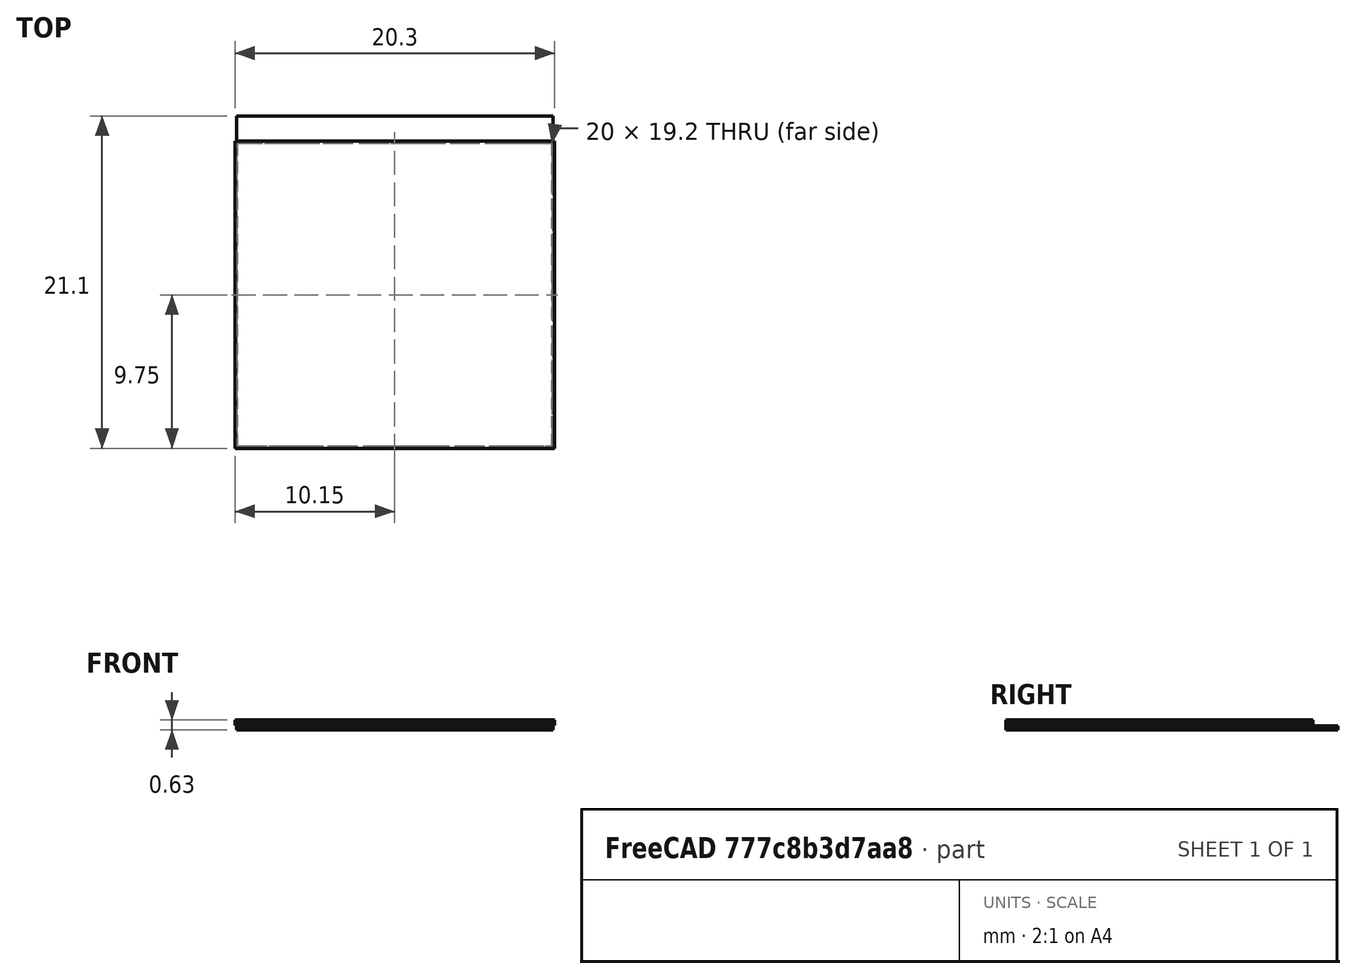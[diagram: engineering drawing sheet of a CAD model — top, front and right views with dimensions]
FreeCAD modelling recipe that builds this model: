
FCSTD DOCUMENT  (FreeCAD 0.17R13541 (Git))
Label: singlethick
License: All rights reserved
LicenseURL: http://en.wikipedia.org/wiki/All_rights_reserved
objects: Sketcher::SketchObject×10, PartDesign::Pad×10, PartDesign::Body×10, PartDesign::ShapeBinder×9, App::MaterialObjectPython×7, Part::FeaturePython×2, Fem::FemSolverObjectPython×1, Fem::ConstraintInitialTemperature×1, Fem::FemMeshObjectPython×1, Fem::ConstraintHeatflux×1, Fem::ConstraintFixed×1, Fem::FemAnalysis×1
note: 51 computed .brp shape members not serialized (recipe doc carries the construction recipe); baked Part::Feature solids carry a one-line shape summary decoded from their .brp

FEATURE [Sketcher::SketchObject] Sketch
  MapMode = 5
  Support = -> [XY_Plane]
  sketch-geometry (4):
    g0: LineSegment StartX=0 StartY=0 StartZ=0 EndX=20.1 EndY=0 EndZ=0
    g1: LineSegment StartX=20.1 StartY=0 StartZ=0 EndX=20.1 EndY=21.1 EndZ=0
    g2: LineSegment StartX=20.1 StartY=21.1 StartZ=0 EndX=0 EndY=21.1 EndZ=0
    g3: LineSegment StartX=0 StartY=21.1 StartZ=0 EndX=0 EndY=0 EndZ=0
  constraints (11):
    c: Coincident(g0,g1)
    c: Coincident(g1,g2)
    c: Coincident(g2,g3)
    c: Coincident(g3,g0)
    c: Horizontal(g0)
    c: Horizontal(g2)
    c: Vertical(g1)
    c: Vertical(g3)
    c: Coincident(g0,g-1)
    c: DistanceX(g0,g0) = 20.1
    c: DistanceY(g3,g3) = 21.1
FEATURE [PartDesign::Pad] Pad
  Length = 0.15
  Length2 = 100
  Profile = -> Sketch
  Type = 0
FEATURE [PartDesign::Body] Body
  Group = -> [Sketch,Pad]
  Origin = -> Origin
  Tip = -> Pad
FEATURE [PartDesign::ShapeBinder] CopyPad
  Placement = pos=(0,0,0.15) rot=(0,0,1;0rad)
FEATURE [Sketcher::SketchObject] Sketch001
  MapMode = 5
  Placement = pos=(0,0,0.15) rot=(0,0,1;0rad)
  Support = -> [CopyPad]
  sketch-geometry (4):
    g0: LineSegment StartX=0.05 StartY=0.15 StartZ=0 EndX=20.05 EndY=0.15 EndZ=0
    g1: LineSegment StartX=20.05 StartY=0.15 StartZ=0 EndX=20.05 EndY=19.35 EndZ=0
    g2: LineSegment StartX=20.05 StartY=19.35 StartZ=0 EndX=0.05 EndY=19.35 EndZ=0
    g3: LineSegment StartX=0.05 StartY=19.35 StartZ=0 EndX=0.05 EndY=0.15 EndZ=0
  constraints (12):
    c: Coincident(g0,g1)
    c: Coincident(g1,g2)
    c: Coincident(g2,g3)
    c: Coincident(g3,g0)
    c: Horizontal(g0)
    c: Horizontal(g2)
    c: Vertical(g1)
    c: Vertical(g3)
    c: DistanceY(g-1,g0) = 0.15
    c: DistanceX(g-1,g0) = 0.05
    c: DistanceX(g0,g0) = 20
    c: DistanceY(g3,g3) = 19.2
FEATURE [PartDesign::Pad] Pad001
  Length = 0.025
  Length2 = 100
  Placement = pos=(0,0,0.15) rot=(0,0,1;0rad)
  Profile = -> Sketch001
  Type = 0
FEATURE [PartDesign::Body] Body001
  Group = -> [CopyPad,Sketch001,Pad001]
  Origin = -> Origin001
  Tip = -> Pad001
FEATURE [PartDesign::ShapeBinder] CopyPad001
  Placement = pos=(0,0,0.025) rot=(0,0,1;0rad)
FEATURE [Sketcher::SketchObject] Sketch002
  MapMode = 5
  Placement = pos=(0,0,0.175) rot=(0,0,1;0rad)
  Support = -> [CopyPad001]
  sketch-geometry (4):
    g0: LineSegment StartX=-0.1 StartY=0 StartZ=0 EndX=20.2 EndY=0 EndZ=0
    g1: LineSegment StartX=20.2 StartY=0 StartZ=0 EndX=20.2 EndY=19.5 EndZ=0
    g2: LineSegment StartX=20.2 StartY=19.5 StartZ=0 EndX=-0.1 EndY=19.5 EndZ=0
    g3: LineSegment StartX=-0.1 StartY=19.5 StartZ=0 EndX=-0.1 EndY=0 EndZ=0
  constraints (12):
    c: Coincident(g0,g1)
    c: Coincident(g1,g2)
    c: Coincident(g2,g3)
    c: Coincident(g3,g0)
    c: Horizontal(g0)
    c: Horizontal(g2)
    c: Vertical(g1)
    c: Vertical(g3)
    c: DistanceY(g0,g-1) = 0
    c: DistanceX(g0,g-1) = 0.1
    c: DistanceX(g0,g0) = 20.3
    c: DistanceY(g3,g3) = 19.5
FEATURE [PartDesign::Pad] Pad002
  Length = 0.15
  Length2 = 100
  Placement = pos=(0,0,0.025) rot=(0,0,1;0rad)
  Profile = -> Sketch002
  Type = 0
FEATURE [PartDesign::Body] Body002
  Group = -> [CopyPad001,Sketch002,Pad002]
  Origin = -> Origin002
  Tip = -> Pad002
FEATURE [PartDesign::ShapeBinder] CopyPad002
  Placement = pos=(0,0,0.15) rot=(0,0,1;0rad)
FEATURE [Sketcher::SketchObject] Sketch003
  MapMode = 5
  Placement = pos=(0,0,0.325) rot=(0,0,1;0rad)
  Support = -> [CopyPad002]
  sketch-geometry (4):
    g0: LineSegment StartX=-0.1 StartY=0 StartZ=0 EndX=20.2 EndY=0 EndZ=0
    g1: LineSegment StartX=20.2 StartY=0 StartZ=0 EndX=20.2 EndY=19.5 EndZ=0
    g2: LineSegment StartX=20.2 StartY=19.5 StartZ=0 EndX=-0.1 EndY=19.5 EndZ=0
    g3: LineSegment StartX=-0.1 StartY=19.5 StartZ=0 EndX=-0.1 EndY=0 EndZ=0
  constraints (12):
    c: Coincident(g0,g1)
    c: Coincident(g1,g2)
    c: Coincident(g2,g3)
    c: Coincident(g3,g0)
    c: Horizontal(g0)
    c: Horizontal(g2)
    c: Vertical(g1)
    c: Vertical(g3)
    c: DistanceY(g0,g-1) = 0
    c: DistanceX(g0,g-1) = 0.1
    c: DistanceX(g0,g0) = 20.3
    c: DistanceY(g3,g3) = 19.5
FEATURE [PartDesign::Pad] Pad003
  Length = 0.05
  Length2 = 100
  Placement = pos=(0,0,0.15) rot=(0,0,1;0rad)
  Profile = -> Sketch003
  Type = 0
FEATURE [PartDesign::Body] Body003
  Group = -> [CopyPad002,Sketch003,Pad003]
  Origin = -> Origin003
  Tip = -> Pad003
FEATURE [PartDesign::ShapeBinder] CopyPad003
  Placement = pos=(0,0,0.05) rot=(0,0,1;0rad)
FEATURE [Sketcher::SketchObject] Sketch004
  MapMode = 5
  Placement = pos=(0,0,0.375) rot=(0,0,1;0rad)
  Support = -> [CopyPad003]
  sketch-geometry (4):
    g0: LineSegment StartX=-0.1 StartY=0 StartZ=0 EndX=20.2 EndY=0 EndZ=0
    g1: LineSegment StartX=20.2 StartY=0 StartZ=0 EndX=20.2 EndY=19.5 EndZ=0
    g2: LineSegment StartX=20.2 StartY=19.5 StartZ=0 EndX=-0.1 EndY=19.5 EndZ=0
    g3: LineSegment StartX=-0.1 StartY=19.5 StartZ=0 EndX=-0.1 EndY=0 EndZ=0
  constraints (12):
    c: Coincident(g0,g1)
    c: Coincident(g1,g2)
    c: Coincident(g2,g3)
    c: Coincident(g3,g0)
    c: Horizontal(g0)
    c: Horizontal(g2)
    c: Vertical(g1)
    c: Vertical(g3)
    c: DistanceX(g0,g-1) = 0.1
    c: DistanceY(g0,g-1) = 0
    c: DistanceX(g0,g0) = 20.3
    c: DistanceY(g3,g3) = 19.5
FEATURE [PartDesign::Pad] Pad004
  Length = 0.0225
  Length2 = 100
  Placement = pos=(0,0,0.05) rot=(0,0,1;0rad)
  Profile = -> Sketch004
  Type = 0
FEATURE [PartDesign::Body] Body004
  Group = -> [CopyPad003,Sketch004,Pad004]
  Origin = -> Origin004
  Tip = -> Pad004
FEATURE [PartDesign::ShapeBinder] CopyPad004
  Placement = pos=(0,0,0.0225) rot=(0,0,1;0rad)
FEATURE [Sketcher::SketchObject] Sketch005
  MapMode = 5
  Placement = pos=(0,0,0.3975) rot=(0,0,1;0rad)
  Support = -> [CopyPad004]
  sketch-geometry (4):
    g0: LineSegment StartX=-0.1 StartY=0 StartZ=0 EndX=20.2 EndY=0 EndZ=0
    g1: LineSegment StartX=20.2 StartY=0 StartZ=0 EndX=20.2 EndY=19.5 EndZ=0
    g2: LineSegment StartX=20.2 StartY=19.5 StartZ=0 EndX=-0.1 EndY=19.5 EndZ=0
    g3: LineSegment StartX=-0.1 StartY=19.5 StartZ=0 EndX=-0.1 EndY=0 EndZ=0
  constraints (12):
    c: Coincident(g0,g1)
    c: Coincident(g1,g2)
    c: Coincident(g2,g3)
    c: Coincident(g3,g0)
    c: Horizontal(g0)
    c: Horizontal(g2)
    c: Vertical(g1)
    c: Vertical(g3)
    c: DistanceY(g0,g-1) = 0
    c: DistanceX(g0,g-1) = 0.1
    c: DistanceX(g0,g0) = 20.3
    c: DistanceY(g3,g3) = 19.5
FEATURE [PartDesign::Pad] Pad005
  Length = 0.0175
  Length2 = 100
  Placement = pos=(0,0,0.0225) rot=(0,0,1;0rad)
  Profile = -> Sketch005
  Type = 0
FEATURE [PartDesign::Body] Body005
  Group = -> [CopyPad004,Sketch005,Pad005]
  Origin = -> Origin005
  Tip = -> Pad005
FEATURE [PartDesign::ShapeBinder] CopyPad005
  Placement = pos=(0,0,0.0175) rot=(0,0,1;0rad)
FEATURE [Sketcher::SketchObject] Sketch006
  MapMode = 5
  Placement = pos=(0,0,0.415) rot=(0,0,1;0rad)
  Support = -> [CopyPad005]
  sketch-geometry (4):
    g0: LineSegment StartX=-0.1 StartY=0 StartZ=0 EndX=20.2 EndY=0 EndZ=0
    g1: LineSegment StartX=20.2 StartY=0 StartZ=0 EndX=20.2 EndY=19.5 EndZ=0
    g2: LineSegment StartX=20.2 StartY=19.5 StartZ=0 EndX=-0.1 EndY=19.5 EndZ=0
    g3: LineSegment StartX=-0.1 StartY=19.5 StartZ=0 EndX=-0.1 EndY=0 EndZ=0
  constraints (12):
    c: Coincident(g0,g1)
    c: Coincident(g1,g2)
    c: Coincident(g2,g3)
    c: Coincident(g3,g0)
    c: Horizontal(g0)
    c: Horizontal(g2)
    c: Vertical(g1)
    c: Vertical(g3)
    c: DistanceY(g0,g-1) = 0
    c: DistanceX(g0,g-1) = 0.1
    c: DistanceX(g0,g0) = 20.3
    c: DistanceY(g3,g3) = 19.5
FEATURE [PartDesign::Pad] Pad006
  Length = 0.07
  Length2 = 100
  Placement = pos=(0,0,0.0175) rot=(0,0,1;0rad)
  Profile = -> Sketch006
  Type = 0
FEATURE [PartDesign::Body] Body006
  Group = -> [CopyPad005,Sketch006,Pad006]
  Origin = -> Origin006
  Tip = -> Pad006
FEATURE [PartDesign::ShapeBinder] CopyPad008
FEATURE [Sketcher::SketchObject] Sketch009
  MapMode = 5
  Placement = pos=(0,0,0) rot=(1,0,0;3.14159rad)
  Support = -> [CopyPad008]
  sketch-geometry (4):
    g0: LineSegment StartX=0 StartY=0 StartZ=0 EndX=20.1 EndY=0 EndZ=0
    g1: LineSegment StartX=20.1 StartY=0 StartZ=0 EndX=20.1 EndY=-21.1 EndZ=0
    g2: LineSegment StartX=20.1 StartY=-21.1 StartZ=0 EndX=0 EndY=-21.1 EndZ=0
    g3: LineSegment StartX=0 StartY=-21.1 StartZ=0 EndX=0 EndY=0 EndZ=0
  constraints (11):
    c: Coincident(g0,g1)
    c: Coincident(g1,g2)
    c: Coincident(g2,g3)
    c: Coincident(g3,g0)
    c: Horizontal(g0)
    c: Horizontal(g2)
    c: Vertical(g1)
    c: Vertical(g3)
    c: Coincident(g0,g-1)
    c: DistanceX(g2,g2) = 20.1
    c: DistanceY(g3,g3) = 21.1
FEATURE [PartDesign::Pad] Pad009
  Length = 0.1
  Length2 = 100
  Profile = -> Sketch009
  Type = 0
FEATURE [PartDesign::Body] Body009
  Group = -> [CopyPad008,Sketch009,Pad009]
  Origin = -> Origin009
  Tip = -> Pad009
FEATURE [Fem::FemSolverObjectPython] CalculiXccxTools  # FEM object (typed FeaturePython)
  AnalysisType = 2
  BeamShellResultOutput3D = false
  EigenmodeHighLimit = 1000000
  EigenmodeLowLimit = 0
  EigenmodesCount = 10
  GeometricalNonlinearity = 0
  IterationsControlParameterCutb = 0.25,0.5,0.75,0.85,,,1.5,
  IterationsControlParameterIter = 4,8,9,200,10,400,,200,,
  IterationsControlParameterTimeUse = false
  IterationsThermoMechMaximum = 2000
  IterationsUserDefinedIncrementations = false
  IterationsUserDefinedTimeStepLength = false
  MaterialNonlinearity = 0
  MatrixSolverType = 0
  SplitInputWriter = false
  ThermoMechSteadyState = true
  TimeEnd = 1
  TimeInitialStep = 0.01
FEATURE [Fem::ConstraintInitialTemperature] FemConstraintInitialTemperature
  NormalDirection = (0,0,1)
  initialTemperature = 300
FEATURE [PartDesign::ShapeBinder] CopyPad006
  Placement = pos=(0,0,0.07) rot=(0,0,1;0rad)
FEATURE [Sketcher::SketchObject] Sketch010
  MapMode = 5
  Placement = pos=(0,0,0.485) rot=(0,0,1;0rad)
  Support = -> [CopyPad006]
  sketch-geometry (4):
    g0: LineSegment StartX=-0.1 StartY=0 StartZ=0 EndX=20.2 EndY=0 EndZ=0
    g1: LineSegment StartX=20.2 StartY=0 StartZ=0 EndX=20.2 EndY=19.5 EndZ=0
    g2: LineSegment StartX=20.2 StartY=19.5 StartZ=0 EndX=-0.1 EndY=19.5 EndZ=0
    g3: LineSegment StartX=-0.1 StartY=19.5 StartZ=0 EndX=-0.1 EndY=0 EndZ=0
  constraints (12):
    c: Coincident(g0,g1)
    c: Coincident(g1,g2)
    c: Coincident(g2,g3)
    c: Coincident(g3,g0)
    c: Horizontal(g0)
    c: Horizontal(g2)
    c: Vertical(g1)
    c: Vertical(g3)
    c: DistanceY(g0,g-1) = 0
    c: DistanceX(g0,g-1) = 0.1
    c: DistanceX(g0,g0) = 20.3
    c: DistanceY(g1,g1) = 19.5
FEATURE [PartDesign::Pad] Pad010
  Length = 0.0175
  Length2 = 100
  Placement = pos=(0,0,0.07) rot=(0,0,1;0rad)
  Profile = -> Sketch010
  Type = 0
FEATURE [PartDesign::Body] Body010
  Group = -> [CopyPad006,Sketch010,Pad010]
  Origin = -> Origin010
  Tip = -> Pad010
FEATURE [PartDesign::ShapeBinder] CopyPad010
  Placement = pos=(0,0,0.0175) rot=(0,0,1;0rad)
FEATURE [Sketcher::SketchObject] Sketch011
  MapMode = 5
  Placement = pos=(0,0,0.5025) rot=(0,0,1;0rad)
  Support = -> [CopyPad010]
  sketch-geometry (4):
    g0: LineSegment StartX=-0.1 StartY=0 StartZ=0 EndX=20.2 EndY=0 EndZ=0
    g1: LineSegment StartX=20.2 StartY=0 StartZ=0 EndX=20.2 EndY=19.5 EndZ=0
    g2: LineSegment StartX=20.2 StartY=19.5 StartZ=0 EndX=-0.1 EndY=19.5 EndZ=0
    g3: LineSegment StartX=-0.1 StartY=19.5 StartZ=0 EndX=-0.1 EndY=0 EndZ=0
  constraints (12):
    c: Coincident(g0,g1)
    c: Coincident(g1,g2)
    c: Coincident(g2,g3)
    c: Coincident(g3,g0)
    c: Horizontal(g0)
    c: Horizontal(g2)
    c: Vertical(g1)
    c: Vertical(g3)
    c: DistanceY(g0,g-1) = 0
    c: DistanceX(g0,g-1) = 0.1
    c: DistanceX(g0,g0) = 20.3
    c: DistanceY(g3,g3) = 19.5
FEATURE [PartDesign::Pad] Pad011
  Length = 0.0225
  Length2 = 100
  Placement = pos=(0,0,0.0175) rot=(0,0,1;0rad)
  Profile = -> Sketch011
  Type = 0
FEATURE [PartDesign::Body] Body011
  Group = -> [CopyPad010,Sketch011,Pad011]
  Origin = -> Origin011
  Tip = -> Pad011
FEATURE [Part::FeaturePython] BooleanFragments  # WARN: FeaturePython — macro-defined, semantics opaque (R4)
  Mode = 2
  Objects = -> [Body009,Body011,Body010,Body006,Body005,Body004,Body003,Body002,Body001,Body]
  Tolerance = 0
FEATURE [Part::FeaturePython] CompoundFilter  # WARN: FeaturePython — macro-defined, semantics opaque (R4)
  Base = -> BooleanFragments
  FilterType = 3
  Invert = false
  OverrideMaxVal = 0
  WindowFrom = 80
  WindowTo = 100
FEATURE [Fem::FemMeshObjectPython] FEMMeshGmsh  # FEM object (typed FeaturePython)
  Algorithm2D = 0
  Algorithm3D = 0
  CharacteristicLengthMax = 2
  CharacteristicLengthMin = 0
  CoherenceMesh = true
  ElementDimension = 0
  ElementOrder = 1
  GeometryTolerance = 1e-06
  GroupsOfNodes = false
  HighOrderOptimize = false
  OptimizeNetgen = false
  OptimizeStd = true
  Part = -> CompoundFilter
  RecombineAll = false
FEATURE [Fem::ConstraintHeatflux] FemConstraintHeatflux
  AmbientTemp = 213
  ConstraintType = 1
  DFlux = 0
  FilmCoef = 10
  NormalDirection = (0,0,1)
  Normals = (394) [(0,0,1),(0,0,1),(0,0,1),(0,0,1),(0,0,1),(0,0,1),(0,0,1),(0,0,1),(0,0,1),(0,0,1),(0,0,1),(0,0,1),(0,0,1),(0,0,1),(0,0,1),(0,0,1),(0,0,1),(1,0,0),+376 more]
  Points = (394) [(-0.1,0,0.525),(10.05,0,0.525),(20.2,0,0.525),(-0.1,9.75,0.525),(10.05,9.75,0.525),(20.2,9.75,0.525),(-0.1,19.5,0.525),(10.05,19.5,0.525),+386 more]
  References = -> [CompoundFilter]
FEATURE [Fem::ConstraintFixed] FemConstraintFixed
  NormalDirection = (0,0,-1)
  Normals = (9) [(0,0,-1),(0,0,-1),(0,0,-1),(0,0,-1),(0,0,-1),(0,0,-1),(0,0,-1),(0,0,-1),(0,0,-1)]
  Points = (9) [(0,0,-0.1),(10.05,0,-0.1),(20.1,0,-0.1),(0,10.55,-0.1),(10.05,10.55,-0.1),(20.1,10.55,-0.1),(0,21.1,-0.1),(10.05,21.1,-0.1),(20.1,21.1,-0.1)]
  References = -> [CompoundFilter]
FEATURE [App::MaterialObjectPython] SolidMaterial  # material (typed FeaturePython)
  Category = 0
  Material = Density=2329.0 kg/m^3,Description=This is a not defined material,Father=None,Name=None,PoissonRatio=0.28,SpecificHeat=0.71 J/kg/K,SpecificPrice=0,+4 more (map truncated)
  References = -> [CompoundFilter]
FEATURE [App::MaterialObjectPython] SolidMaterial001  # material (typed FeaturePython)
  Category = 0
  Material = Density=2.356e+12 kg/m^3,Description=This is a not defined material,Father=None,Name=None,PoissonRatio=0.35,SpecificHeat=0.8 J/kg/K,SpecificPrice=0,+4 more (map truncated)
  References = -> [CompoundFilter]
FEATURE [App::MaterialObjectPython] SolidMaterial002  # material (typed FeaturePython)
  Category = 0
  Material = Density=1500.0 kg/m^3,Description=This is a not defined material,Father=None,Name=None,PoissonRatio=0.34,SpecificHeat=0.21 J/kg/K,SpecificPrice=0,+4 more (map truncated)
  References = -> [CompoundFilter]
FEATURE [App::MaterialObjectPython] SolidMaterial003  # material (typed FeaturePython)
  Category = 0
  Material = Density=142.0 kg/m^3,Description=This is a not defined material,Father=None,Name=None,PoissonRatio=0.34,SpecificHeat=1.09 J/kg/K,SpecificPrice=0,+4 more (map truncated)
  References = -> [CompoundFilter]
FEATURE [App::MaterialObjectPython] SolidMaterial004  # material (typed FeaturePython)
  Category = 0
  Material = Density=2809.7 kg/m^3,Description=This is a not defined material,Father=None,Name=None,PoissonRatio=0.341,SpecificHeat=0.8433 J/kg/K,SpecificPrice=0,+4 more (map truncated)
  References = -> [CompoundFilter]
FEATURE [App::MaterialObjectPython] SolidMaterial005  # material (typed FeaturePython)
  Category = 0
  Material = Density=7764.0 kg/m^3,Description=This is a not defined material,Father=None,Name=None,PoissonRatio=0.343,SpecificHeat=0.385 J/kg/K,SpecificPrice=0,+4 more (map truncated)
  References = -> [CompoundFilter]
FEATURE [App::MaterialObjectPython] SolidMaterial006  # material (typed FeaturePython)
  Category = 0
  Material = Density=1000.0 kg/m^3,Description=This is a not defined material,Father=None,Name=None,PoissonRatio=0.35,SpecificHeat=0.8 J/kg/K,SpecificPrice=0,+4 more (map truncated)
  References = -> [CompoundFilter]
FEATURE [Fem::FemAnalysis] Analysis
  Group = -> [CalculiXccxTools,FemConstraintInitialTemperature,FEMMeshGmsh,FemConstraintHeatflux,FemConstraintFixed,SolidMaterial,SolidMaterial001,SolidMaterial002,SolidMaterial003,SolidMaterial004,SolidMaterial005,SolidMaterial006]
